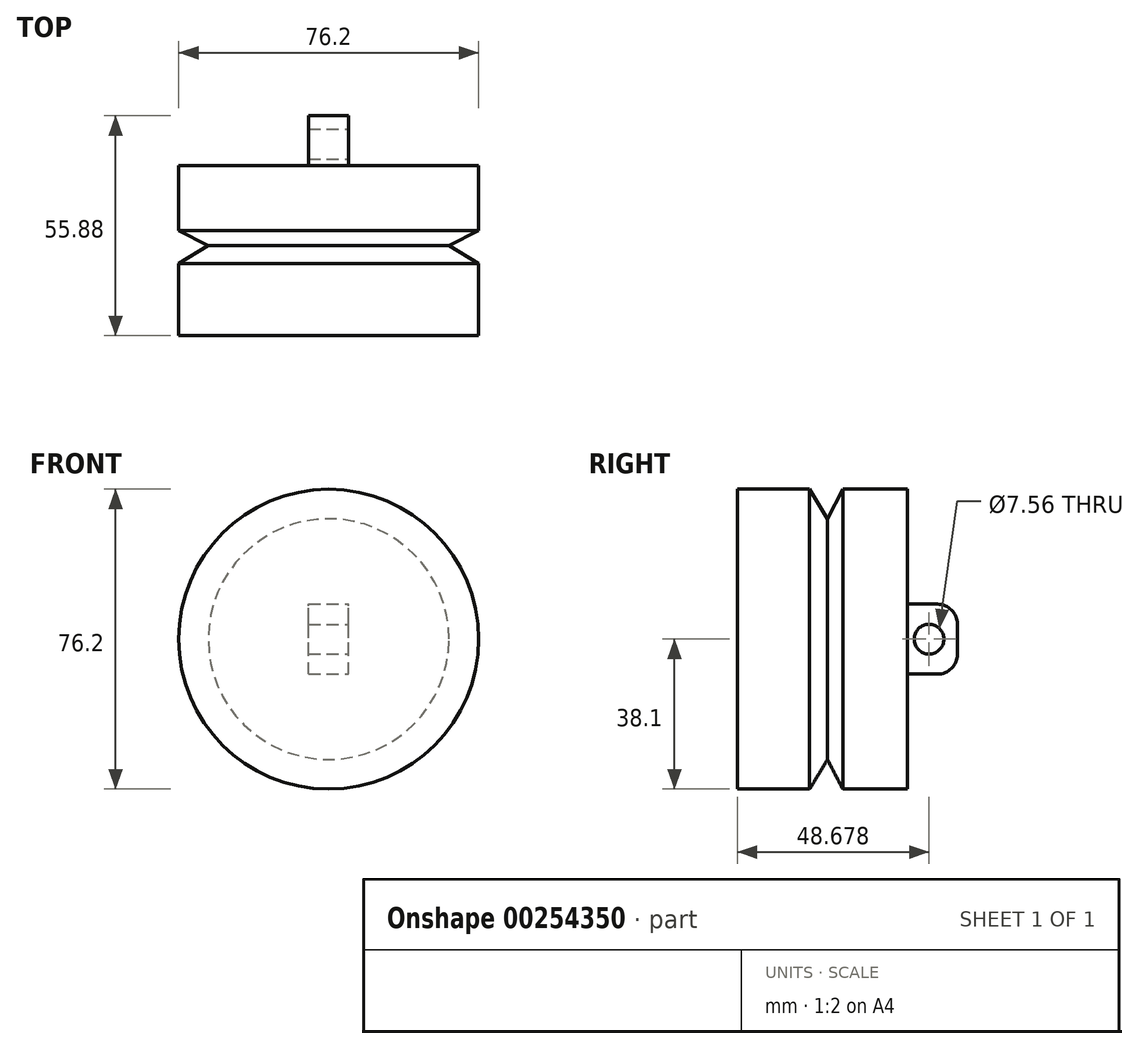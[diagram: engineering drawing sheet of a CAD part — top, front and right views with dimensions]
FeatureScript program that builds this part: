
annotation { "Feature Type Name" : "Feature", "Feature Type Description" : "" }
export const myFeature = defineFeature(function(context is Context, id is Id, definition is map)
    precondition{}
    {
        {
            var Q0;
            Q0=qCreatedBy(makeId("Top.planeOp"),FACE);
            var sketch = newSketch(context, id + "F0", { "sketchPlane" : qUnion([Q0])});
            skLineSegment(sketch, "E0", {"start": v(38.1, 0) * mm, "end": v(38.1, 18.35) * mm});
            skLineSegment(sketch, "E1", {"start": v(38.1, 18.35) * mm, "end": v(30.58, 22.86) * mm});
            skLineSegment(sketch, "E2", {"start": v(30.58, 22.86) * mm, "end": v(38.1, 26.77) * mm});
            skLineSegment(sketch, "E3", {"start": v(38.1, 26.77) * mm, "end": v(38.1, 43.18) * mm});
            skLineSegment(sketch, "E4", {"start": v(0, 0) * mm, "end": v(0, 43.18) * mm});
            skLineSegment(sketch, "E5", {"start": v(0, 0) * mm, "end": v(38.1, 0) * mm});
            skLineSegment(sketch, "E6", {"start": v(38.1, 43.18) * mm, "end": v(0, 43.18) * mm});
            skSolve(sketch);
        }
        {
            var Q0;
            Q0=makeQuery(id+"F0.imprint","IMPRINT",FACE,{"disambiguationData":[TD([[makeQuery(id+"F0.imprint","IMPRINT",EDGE,{"derivedFrom":sQuery(id+"F0.wireOp",EDGE,"E0")}),1.0]])]});
            var Q1;
            Q1=sQuery(id+"F0.wireOp",EDGE,"E4");
            revolve(context, id + "F1", {"entities" : qUnion([Q0]), "axis" : qUnion([Q1]), "revolveType" : RevolveType.FULL});
        }
        {
            var Q0;
            Q0=makeQuery(id+"F1.opRevolve","SWEPT_FACE",FACE,{"disambiguationData":[OSD([sQuery(id+"F0.wireOp",EDGE,"E6")])]});
            var sketch = newSketch(context, id + "F2", { "sketchPlane" : qUnion([Q0])});
            skLineSegment(sketch, "E7.bottom", {"start": v(5.08, -8.89) * mm, "end": v(-5.08, -8.89) * mm});
            skLineSegment(sketch, "E7.top", {"start": v(5.08, 8.9) * mm, "end": v(-5.08, 8.9) * mm});
            skLineSegment(sketch, "E7.left", {"start": v(5.08, -8.89) * mm, "end": v(5.08, 8.9) * mm});
            skLineSegment(sketch, "E7.right", {"start": v(-5.08, -8.89) * mm, "end": v(-5.08, 8.9) * mm});
            skPoint(sketch, "E7.middle", {"position": v(0, 0) * mm});
            skSolve(sketch);
        }
        {
            var Q0;
            Q0=makeQuery(id+"F2.imprint","IMPRINT",FACE,{"disambiguationData":[TD([[makeQuery(id+"F2.imprint","IMPRINT",EDGE,{"derivedFrom":sQuery(id+"F2.wireOp",EDGE,"E7.bottom")}),-1.0]])]});
            extrude(context, id + "F3", {"entities" : qUnion([Q0]), "operationType" : NewBodyOperationType.ADD, "depth" : 12.7 * mm});
        }
        {
            var Q0;
            Q0=makeQuery(id+"F3.opExtrude","CAP_EDGE",EDGE,{"disambiguationData":[OSD([sQuery(id+"F2.wireOp",EDGE,"E7.top")])],"isStart":false});
            var Q1;
            Q1=makeQuery(id+"F3.opExtrude","CAP_EDGE",EDGE,{"disambiguationData":[OSD([sQuery(id+"F2.wireOp",EDGE,"E7.bottom")])],"isStart":false});
            fillet(context, id + "F4", {"entities" : qUnion([Q0, Q1]), "radius" : 5.08 * mm, "tangentPropagation" : true, "allowEdgeOverflow" : false});
        }
        {
            var Q0;
            Q0=makeQuery(id+"F3.opExtrude","SWEPT_FACE",FACE,{"disambiguationData":[OSD([sQuery(id+"F2.wireOp",EDGE,"E7.right")])]});
            var sketch = newSketch(context, id + "F5", { "sketchPlane" : qUnion([Q0])});
            skCircle(sketch, "E8", {"center": v(48.68, 0) * mm, "radius": 3.78 * mm});
            skSolve(sketch);
        }
        {
            var Q0;
            Q0 = qSketchRegion(id + "F5", true);
            extrude(context, id + "F6", {"entities" : qUnion([Q0]), "operationType" : NewBodyOperationType.REMOVE, "oppositeDirection" : true, "depth" : 25.4 * mm});
        }
    });
